# Revit family: 0005363-3000K
name_source: partatom
category: Lighting Fixtures
revit_build: Autodesk Revit 2018 (Build: 20170223_1515(x64)
units: mm (PartAtom-declared; Revit-internal decimal feet)

## family parameters
Cut with Voids When Loaded = No
Host = Face
Light Source = Yes
OmniClass Number = 23.80.70.00
OmniClass Title = Lighting
Part Type = Normal
Room Calculation Point = No
Round Connector Dimension = Use Diameter
Shared = No

## types (1)
- 0005363 OBICO 68 IP65 550LM 3CCT DIM ADJ WHT
    Apparent Load = 5 VA
    Assembly Code = D5020200
    AssetType = Fixed
    ClassificationName = Uniclass2015
    ClassificationValue = EF_70_80
    Color Filter = 16777215
    Cost = 0 $
    Default Elevation = 1219 mm
    Description = OBICO 68 IP65 550lm 3CCT DIM ADJ WHITE
    Dimming Lamp Color Temperature Shift = <None>
    DocumentationLiterature = http://www.sylvania-lighting.com
    ElectricShockClassification = 102
    Emit Shape Visible in Rendering = No
    Emit from Circle Diameter = 610 mm
    IfcExportAs = Class II
    IfcExportType = IfcLightFixtureType
    ImpactProtectionIndex = IfcLightFixtureType
    IngressProtection = IfcLightFixtureType
    InputNominalFrequency = 3000
    InputVoltage = 0
    LampColourRenderingIndex = 16500
    LampColourTemperature = LED
    LampMacAdamStep = 90
    LampNominalLuminous = 3000 K
    LightOutputRatio = LED
    LuminaireType = 0
    ManufacturerName = 102 lm/W
    Material = Feilo Sylvania
    Material_1_SYL = Default
    Material_2_SYL = <By Category>
    Material_3_SYL = <By Category>
    Material_4_SYL = <By Category>
    Model = OBICO 68 IP65 550lm 3CCT DIM ADJ WHITE
    ModelNumber = 0005363
    ModelReference = OBICO 68 IP65 550lm 3CCT DIM ADJ WHITE
    Name = OBICO 68 IP65 550lm 3CCT DIM ADJ WHITE
    NominalDepth = 96 mm  [stored 0.314961 ft]
    NominalHeight = 54 mm  [stored 0.177165 ft]
    NominalLength = 117 mm  [stored 0.383858 ft]
    Photometric Web File = 0005363-2700K.ies
    PowerConsumption = Lighting
    PowerFactor = 0.9
    Tilt Angle = -90.00°
    Type Image = <None>
    TypeName = OBICO 68 IP65 550lm 3CCT DIM ADJ WHITE
    URL = 0.8
    Voltage = 0 V
    WarrantyDescription = http://www.sylvania-lighting.com

note: [stored X ft] marks values corroborated as IEEE doubles in the binary element streams (Revit-internal decimal feet)

## geometry (parser evidence)
native form markers: Blend x2, Sweep x3
no freeform markers — native parametric forms only
